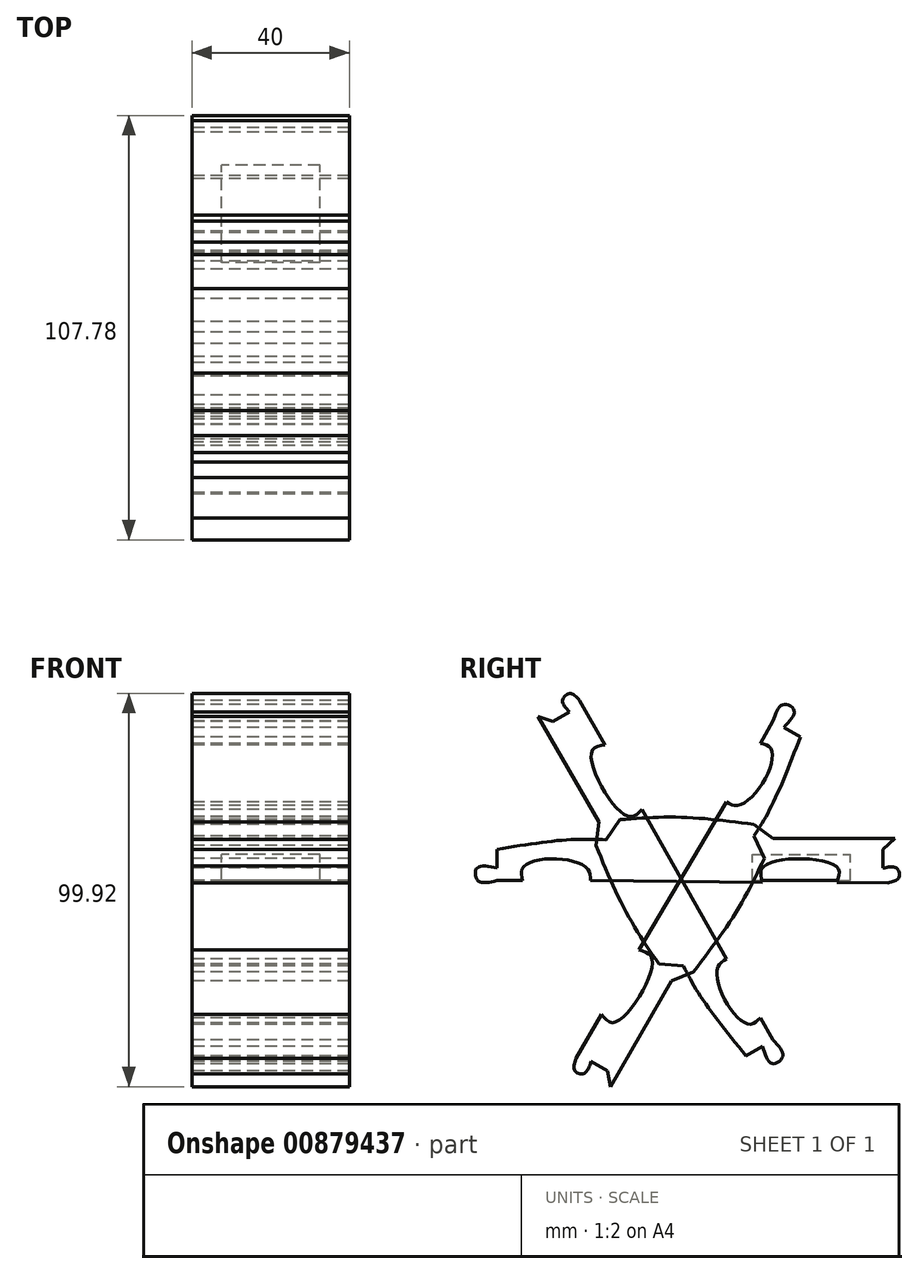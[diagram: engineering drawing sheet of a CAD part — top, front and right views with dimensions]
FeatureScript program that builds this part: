
annotation { "Feature Type Name" : "Feature", "Feature Type Description" : "" }
export const myFeature = defineFeature(function(context is Context, id is Id, definition is map)
    precondition{}
    {
        {
            var Q0;
            Q0=qCreatedBy(makeId("Right.planeOp"),FACE);
            var sketch = newSketch(context, id + "F0", { "sketchPlane" : qUnion([Q0])});
            skFitSpline(sketch, "E0", {"points": [v(18.5, 14.29) * mm, v(0, 16.1) * mm, v(-15.5, 15.5) * mm], "startDerivative": vector(-36.16, 4.68) * mm, "endDerivative": vector(-31.75, -2.39) * mm});
            skFitSpline(sketch, "E1", {"points": [v(-15.5, 15.5) * mm, v(-19.1, 10.38) * mm], "startDerivative": vector(-3.6, -5.11) * mm, "endDerivative": vector(-3.6, -5.11) * mm});
            skFitSpline(sketch, "E2", {"points": [v(-19.1, 10.38) * mm, v(-28.73, 10.38) * mm, v(-46.77, 7.97) * mm], "startDerivative": vector(-21.12, 0.87) * mm, "endDerivative": vector(-33.57, -5.36) * mm});
            skFitSpline(sketch, "E3", {"points": [v(-46.77, 7.97) * mm, v(-46.77, 3.16) * mm], "startDerivative": vector(0, -4.81) * mm, "endDerivative": vector(0, -4.81) * mm});
            skFitSpline(sketch, "E4", {"points": [v(-46.77, 3.16) * mm, v(-51.89, 3.16) * mm, v(-51.59, 0) * mm, v(-46.77, 0) * mm], "startDerivative": vector(-17.73, 3.98) * mm, "endDerivative": vector(16.38, 3.92) * mm});
            skFitSpline(sketch, "E5", {"points": [v(-46.77, 0) * mm, v(-40.3, 0) * mm], "startDerivative": vector(6.48, 0) * mm, "endDerivative": vector(6.48, 0) * mm});
            skFitSpline(sketch, "E6", {"points": [v(-40.3, 0) * mm, v(-40.3, 3.16) * mm, v(-32.94, 5.56) * mm, v(-23.91, 3.16) * mm, v(-23.01, 0) * mm], "startDerivative": vector(-4.72, 17.87) * mm, "endDerivative": vector(0.24, -17.52) * mm});
            skFitSpline(sketch, "E7", {"points": [v(-23.01, 0) * mm, v(20.6, -0.46) * mm], "startDerivative": vector(43.61, -0.46) * mm, "endDerivative": vector(43.61, -0.46) * mm});
            skFitSpline(sketch, "E8", {"points": [v(20.6, -0.46) * mm, v(20.6, 3.16) * mm, v(29.33, 5.56) * mm, v(39.85, 3.16) * mm, v(39.55, -0.46) * mm], "startDerivative": vector(-5.4, 20.91) * mm, "endDerivative": vector(-8.1, -20.87) * mm});
            skFitSpline(sketch, "E9", {"points": [v(18.5, 14.29) * mm, v(23.31, 10.68) * mm], "startDerivative": vector(4.81, -3.6) * mm, "endDerivative": vector(4.81, -3.6) * mm});
            skFitSpline(sketch, "E10", {"points": [v(23.31, 10.68) * mm, v(54.3, 10.68) * mm], "startDerivative": vector(30.98, 0) * mm, "endDerivative": vector(30.98, 0) * mm});
            skFitSpline(sketch, "E11", {"points": [v(54.3, 10.68) * mm, v(51.28, 7.97) * mm], "startDerivative": vector(-3, -2.7) * mm, "endDerivative": vector(-3, -2.7) * mm});
            skFitSpline(sketch, "E12", {"points": [v(51.28, 7.97) * mm, v(51.28, 3.16) * mm], "startDerivative": vector(0, -4.81) * mm, "endDerivative": vector(0, -4.81) * mm});
            skFitSpline(sketch, "E13", {"points": [v(52.48, -0.55) * mm, v(39.55, -0.46) * mm], "startDerivative": vector(-12.92, 0.1) * mm, "endDerivative": vector(-12.92, 0.1) * mm});
            skPoint(sketch, "E14.1.internal.orphan", {"position": v(54.3, 3.16) * mm});
            skPoint(sketch, "E14.2.internal.orphan", {"position": v(54.3, -0.46) * mm});
            skPoint(sketch, "E14.3.internal.orphan", {"position": v(51.28, 0) * mm});
            skFitSpline(sketch, "E15", {"points": [v(51.28, 3.16) * mm, v(54.72, 3.16) * mm, v(55.34, 0.75) * mm, v(52.48, -0.55) * mm], "startDerivative": vector(11.1, 2.55) * mm, "endDerivative": vector(-10.86, -2.14) * mm});
            skSolve(sketch);
        }
        {
            var Q0;
            Q0=makeQuery(id+"F0.imprint","IMPRINT",FACE,{"disambiguationData":[TD([[makeQuery(id+"F0.imprint","IMPRINT",EDGE,{"derivedFrom":sQuery(id+"F0.wireOp",EDGE,"E0")}),1.0]])]});
            extrude(context, id + "F1", {"entities" : qUnion([Q0]), "depth" : 40 * mm, "offsetDistance" : 25.4 * mm});
        }
        {
            var Q0;
            Q0=makeQuery(id+"F1.opExtrude","CAP_FACE",FACE,{"disambiguationData":[OSD([sQuery(id+"F0.wireOp",EDGE,"E0"),sQuery(id+"F0.wireOp",EDGE,"E1"),sQuery(id+"F0.wireOp",EDGE,"E2"),sQuery(id+"F0.wireOp",EDGE,"E3"),sQuery(id+"F0.wireOp",EDGE,"E4"),sQuery(id+"F0.wireOp",EDGE,"E5"),sQuery(id+"F0.wireOp",EDGE,"E6"),sQuery(id+"F0.wireOp",EDGE,"E7"),sQuery(id+"F0.wireOp",EDGE,"E8"),sQuery(id+"F0.wireOp",EDGE,"E9"),sQuery(id+"F0.wireOp",EDGE,"E10"),sQuery(id+"F0.wireOp",EDGE,"E11"),sQuery(id+"F0.wireOp",EDGE,"E12"),sQuery(id+"F0.wireOp",EDGE,"E13"),sQuery(id+"F0.wireOp",EDGE,"E15")])],"isStart":false});
            cPlane(context, id + "F2", {"entities" : qUnion([Q0]), "cplaneType" : CPlaneType.OFFSET, "offset" : 20 * mm, "oppositeDirection" : true, "width" : 150 * mm, "height" : 150 * mm});
        }
        {
            var Q0;
            Q0=qCreatedBy(id+"F2.planeOp",FACE);
            var sketch = newSketch(context, id + "F3", { "sketchPlane" : qUnion([Q0])});
            skLineSegment(sketch, "E16.bottom", {"start": v(18.16, 0) * mm, "end": v(42.99, 0) * mm});
            skLineSegment(sketch, "E16.top", {"start": v(18.16, 6.6) * mm, "end": v(42.99, 6.6) * mm});
            skLineSegment(sketch, "E16.left", {"start": v(18.16, 0) * mm, "end": v(18.16, 6.6) * mm});
            skLineSegment(sketch, "E16.right", {"start": v(42.99, 0) * mm, "end": v(42.99, 6.6) * mm});
            skSolve(sketch);
        }
        {
            var Q0;
            Q0=qCreatedBy(makeId("Top.planeOp"),FACE);
            var sketch = newSketch(context, id + "F4", { "sketchPlane" : qUnion([Q0])});
            skLineSegment(sketch, "E17", {"start": v(-5.63, 0) * mm, "end": v(39.91, 0) * mm});
            skSolve(sketch);
        }
        {
            var Q0;
            Q0=makeQuery(id+"F3.imprint","IMPRINT",FACE,{"disambiguationData":[TD([[makeQuery(id+"F3.imprint","IMPRINT",EDGE,{"derivedFrom":sQuery(id+"F3.wireOp",EDGE,"E16.bottom")}),1.0]])]});
            extrude(context, id + "F5", {"entities" : qUnion([Q0]), "endBound" : BoundingType.SYMMETRIC, "depth" : 25 * mm, "offsetDistance" : 25 * mm});
        }
        {
            var Q0;
            Q0=makeQuery(id+"F1.opExtrude","SWEPT_BODY",BODY,{"disambiguationData":[OSD([sQuery(id+"F0.wireOp",EDGE,"E0"),sQuery(id+"F0.wireOp",EDGE,"E1"),sQuery(id+"F0.wireOp",EDGE,"E2"),sQuery(id+"F0.wireOp",EDGE,"E3"),sQuery(id+"F0.wireOp",EDGE,"E4"),sQuery(id+"F0.wireOp",EDGE,"E5"),sQuery(id+"F0.wireOp",EDGE,"E6"),sQuery(id+"F0.wireOp",EDGE,"E7"),sQuery(id+"F0.wireOp",EDGE,"E8"),sQuery(id+"F0.wireOp",EDGE,"E9"),sQuery(id+"F0.wireOp",EDGE,"E10"),sQuery(id+"F0.wireOp",EDGE,"E11"),sQuery(id+"F0.wireOp",EDGE,"E12"),sQuery(id+"F0.wireOp",EDGE,"E13"),sQuery(id+"F0.wireOp",EDGE,"E15")])]});
            var Q1;
            Q1=sQuery(id+"F4.wireOp",EDGE,"E17");
            circularPattern(context, id + "F6", {"entities" : qUnion([Q0]), "axis" : qUnion([Q1]), "angle" : 360 * degree, "instanceCount" : 3, "equalSpace" : true});
        }
    });
